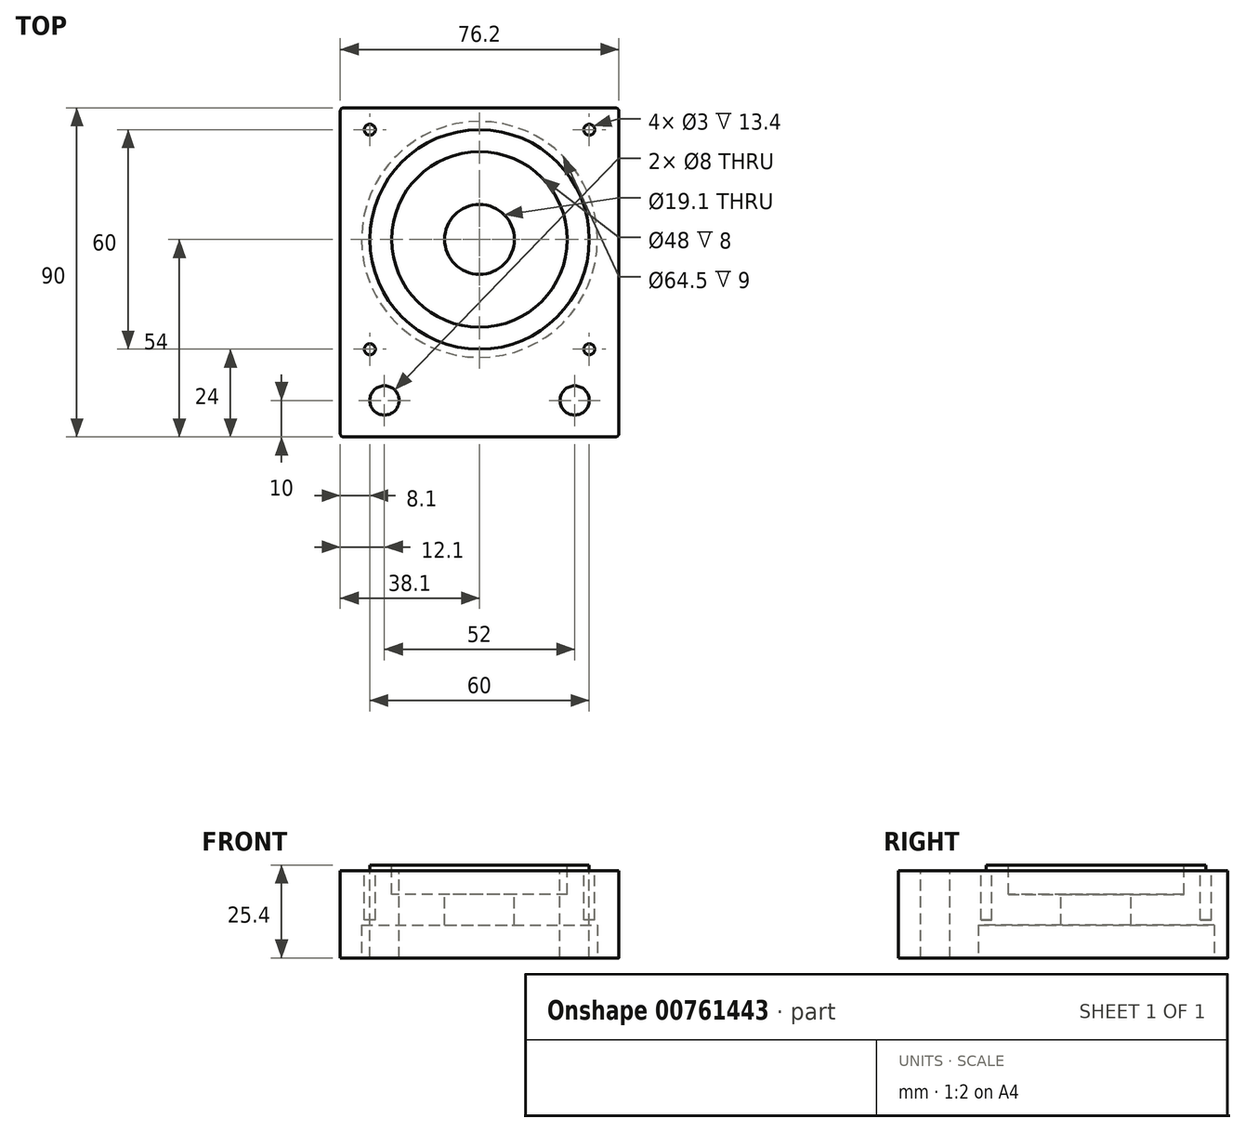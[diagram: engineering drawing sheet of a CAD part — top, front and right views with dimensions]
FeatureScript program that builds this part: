
annotation { "Feature Type Name" : "Feature", "Feature Type Description" : "" }
export const myFeature = defineFeature(function(context is Context, id is Id, definition is map)
    precondition{}
    {
        {
            var Q0;
            Q0=qCreatedBy(makeId("Top.planeOp"),FACE);
            var sketch = newSketch(context, id + "F0", { "sketchPlane" : qUnion([Q0])});
            skLineSegment(sketch, "E0.bottom", {"start": v(0, 0) * mm, "end": v(76.2, 0) * mm});
            skLineSegment(sketch, "E0.top", {"start": v(0, 90) * mm, "end": v(76.2, 90) * mm});
            skLineSegment(sketch, "E0.left", {"start": v(0, 0) * mm, "end": v(0, 90) * mm});
            skLineSegment(sketch, "E0.right", {"start": v(76.2, 0) * mm, "end": v(76.2, 90) * mm});
            skSolve(sketch);
        }
        {
            var Q0;
            Q0=makeQuery(id+"F0.imprint","IMPRINT",FACE,{"disambiguationData":[TD([[makeQuery(id+"F0.imprint","IMPRINT",EDGE,{"derivedFrom":sQuery(id+"F0.wireOp",EDGE,"E0.bottom")}),1.0]])]});
            extrude(context, id + "F1", {"entities" : qUnion([Q0]), "depth" : 25.4 * mm, "offsetDistance" : 25 * mm});
        }
        {
            var Q0;
            Q0=makeQuery(id+"F1.opExtrude","CAP_FACE",FACE,{"disambiguationData":[OSD([sQuery(id+"F0.wireOp",EDGE,"E0.bottom"),sQuery(id+"F0.wireOp",EDGE,"E0.top"),sQuery(id+"F0.wireOp",EDGE,"E0.left"),sQuery(id+"F0.wireOp",EDGE,"E0.right")])],"isStart":false});
            var sketch = newSketch(context, id + "F2", { "sketchPlane" : qUnion([Q0])});
            skCircle(sketch, "E1", {"center": v(38.1, 54) * mm, "radius": 9.55 * mm});
            skCircle(sketch, "E2", {"center": v(12.1, 10) * mm, "radius": 4 * mm});
            skCircle(sketch, "E3", {"center": v(64.1, 10) * mm, "radius": 4 * mm});
            skSolve(sketch);
        }
        {
            var Q0;
            Q0 = qSketchRegion(id + "F2", true);
            extrude(context, id + "F3", {"entities" : qUnion([Q0]), "operationType" : NewBodyOperationType.REMOVE, "endBound" : BoundingType.UP_TO_NEXT, "oppositeDirection" : true, "depth" : 25 * mm, "offsetDistance" : 25 * mm});
        }
        {
            var Q0;
            Q0=makeQuery(id+"F1.opExtrude","CAP_FACE",FACE,{"disambiguationData":[OSD([sQuery(id+"F0.wireOp",EDGE,"E0.bottom"),sQuery(id+"F0.wireOp",EDGE,"E0.top"),sQuery(id+"F0.wireOp",EDGE,"E0.left"),sQuery(id+"F0.wireOp",EDGE,"E0.right")])],"isStart":false});
            var sketch = newSketch(context, id + "F4", { "sketchPlane" : qUnion([Q0])});
            skSolve(sketch);
        }
        {
            var Q0;
            Q0=makeQuery(id+"F4.imprint","IMPRINT",FACE,{"disambiguationData":[TD([[makeQuery(id+"F4.imprint","IMPRINT",EDGE,{"derivedFrom":makeQuery(id+"F1.opExtrude","CAP_EDGE",EDGE,{"disambiguationData":[OSD([sQuery(id+"F0.wireOp",EDGE,"E0.bottom")])],"isStart":false})}),1.0]])]});
            var sketch = newSketch(context, id + "F5", { "sketchPlane" : qUnion([Q0])});
            skCircle(sketch, "E4", {"center": v(8.1, 84) * mm, "radius": 1.5 * mm});
            skCircle(sketch, "E5", {"center": v(68.1, 84) * mm, "radius": 1.5 * mm});
            skCircle(sketch, "E6", {"center": v(68.1, 24) * mm, "radius": 1.5 * mm});
            skCircle(sketch, "E7", {"center": v(8.1, 24) * mm, "radius": 1.5 * mm});
            skSolve(sketch);
        }
        {
            var Q0;
            Q0 = qSketchRegion(id + "F5", true);
            extrude(context, id + "F6", {"entities" : qUnion([Q0]), "operationType" : NewBodyOperationType.REMOVE, "oppositeDirection" : true, "depth" : 15 * mm, "offsetDistance" : 25 * mm});
        }
        {
            var Q0;
            Q0=makeQuery(id+"F4.imprint","IMPRINT",FACE,{"disambiguationData":[TD([[makeQuery(id+"F4.imprint","IMPRINT",EDGE,{"derivedFrom":makeQuery(id+"F1.opExtrude","CAP_EDGE",EDGE,{"disambiguationData":[OSD([sQuery(id+"F0.wireOp",EDGE,"E0.bottom")])],"isStart":false})}),1.0]])]});
            var sketch = newSketch(context, id + "F7", { "sketchPlane" : qUnion([Q0])});
            skCircle(sketch, "E8", {"center": v(38.1, 54) * mm, "radius": 30 * mm});
            skLineSegment(sketch, "E9.bottom", {"start": v(-7.25, 94.02) * mm, "end": v(87.93, 94.02) * mm});
            skLineSegment(sketch, "E9.top", {"start": v(-7.25, -5.8) * mm, "end": v(87.93, -5.8) * mm});
            skLineSegment(sketch, "E9.left", {"start": v(-7.25, 94.02) * mm, "end": v(-7.25, -5.8) * mm});
            skLineSegment(sketch, "E9.right", {"start": v(87.93, 94.02) * mm, "end": v(87.93, -5.8) * mm});
            skSolve(sketch);
        }
        {
            var Q0;
            Q0 = qSketchRegion(id + "F7", true);
            extrude(context, id + "F8", {"entities" : qUnion([Q0]), "operationType" : NewBodyOperationType.REMOVE, "oppositeDirection" : true, "depth" : 1.6 * mm, "offsetDistance" : 25 * mm});
        }
        {
            var Q0;
            Q0=makeQuery(id+"F4.imprint","IMPRINT",FACE,{"disambiguationData":[TD([[makeQuery(id+"F4.imprint","IMPRINT",EDGE,{"derivedFrom":makeQuery(id+"F1.opExtrude","CAP_EDGE",EDGE,{"disambiguationData":[OSD([sQuery(id+"F0.wireOp",EDGE,"E0.bottom")])],"isStart":false})}),1.0]])]});
            var sketch = newSketch(context, id + "F9", { "sketchPlane" : qUnion([Q0])});
            skCircle(sketch, "E10", {"center": v(38.1, 54) * mm, "radius": 24 * mm});
            skSolve(sketch);
        }
        {
            var Q0;
            Q0 = qSketchRegion(id + "F9", true);
            extrude(context, id + "F10", {"entities" : qUnion([Q0]), "operationType" : NewBodyOperationType.REMOVE, "oppositeDirection" : true, "depth" : 8 * mm, "offsetDistance" : 25 * mm});
        }
        {
            var Q0;
            Q0=makeQuery(id+"F1.opExtrude","CAP_FACE",FACE,{"disambiguationData":[OSD([sQuery(id+"F0.wireOp",EDGE,"E0.bottom"),sQuery(id+"F0.wireOp",EDGE,"E0.top"),sQuery(id+"F0.wireOp",EDGE,"E0.left"),sQuery(id+"F0.wireOp",EDGE,"E0.right")])],"isStart":true});
            var sketch = newSketch(context, id + "F11", { "sketchPlane" : qUnion([Q0])});
            skCircle(sketch, "E11", {"center": v(38.1, -54) * mm, "radius": 32.25 * mm});
            skSolve(sketch);
        }
        {
            var Q0;
            Q0 = qSketchRegion(id + "F11", true);
            extrude(context, id + "F12", {"entities" : qUnion([Q0]), "operationType" : NewBodyOperationType.REMOVE, "oppositeDirection" : true, "depth" : 9 * mm, "offsetDistance" : 25 * mm});
        }
        {
            var Q0;
            Q0=makeQuery(id+"F1.opExtrude","SWEPT_EDGE",EDGE,{"disambiguationData":[OSD([sQuery(id+"F0.wireOp",EDGE,"E0.bottom"),sQuery(id+"F0.wireOp",EDGE,"E0.right")])]});
            var Q1;
            Q1=makeQuery(id+"F1.opExtrude","SWEPT_EDGE",EDGE,{"disambiguationData":[OSD([sQuery(id+"F0.wireOp",EDGE,"E0.bottom"),sQuery(id+"F0.wireOp",EDGE,"E0.left")])]});
            var Q2;
            Q2=makeQuery(id+"F1.opExtrude","SWEPT_EDGE",EDGE,{"disambiguationData":[OSD([sQuery(id+"F0.wireOp",EDGE,"E0.top"),sQuery(id+"F0.wireOp",EDGE,"E0.right")])]});
            var Q3;
            Q3=makeQuery(id+"F1.opExtrude","SWEPT_EDGE",EDGE,{"disambiguationData":[OSD([sQuery(id+"F0.wireOp",EDGE,"E0.top"),sQuery(id+"F0.wireOp",EDGE,"E0.left")])]});
            fillet(context, id + "F13", {"entities" : qUnion([Q0, Q1, Q2, Q3]), "radius" : 1 * mm, "tangentPropagation" : true, "allowEdgeOverflow" : false});
        }
    });
